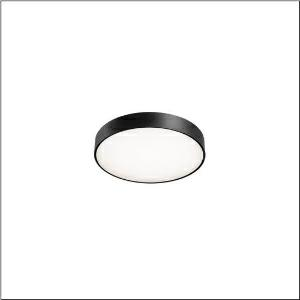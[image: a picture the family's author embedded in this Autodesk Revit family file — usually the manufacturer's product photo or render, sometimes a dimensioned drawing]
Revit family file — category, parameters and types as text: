
# Revit family: round_21_s_51mr34gd0421b
name_source: partatom
category: Lighting Fixtures
units: mm (PartAtom-declared; Revit-internal decimal feet)

## family parameters
Cut with Voids When Loaded = No
Host = Face
Light Source = No
Part Type = Normal
Room Calculation Point = No
Round Connector Dimension = Use Diameter
Shared = No

## types (1)
- Round 21 S (1 x LED, 4090 lm, 28.3 W, 4000K)
    Apparent Load = 28 VA
    CIE Flux Codes = 49 80 96 79 100
    Color Rendering = 80
    Color Temperature = 4000K
    Default Elevation = 1800 mm
    Description = Round 21 S, wall and ceiling luminaire, primary optical cover: cover, of PMMA, opal, light emission: direct/indirect distribution, primary light characteristic: symmetric, installation type: suspended mounting, surface-mounted, LED, rated luminous flux: 4.090lm, luminous efficacy: 135lm/W, light colour: 840, colour temperature: 4000K, control gear: DALI 2, with terminal, 5-pole, mains connection: 230V, AC, 50/60Hz, rated input power: 28.3W, housing, of aluminium, coated, black, diameter: 400mm, height: 62mm, protection rating (complete): IP40, insulation class (complete): insulation class I (protective earthing), certification: CE, impact resistance: IK04, permissible operating ambient temperature: -10..+35°C, packaging unit: 1 piece
    Height = 87 mm
    Lamp = 1 x LED
    Lamp Light Flux = 4090 lm
    Lamp Power = 28.3 W
    Lamp count = 1
    Length = 400 mm
    Luminous efficacy = 145 lm/W
    Manufacturer = Siteco
    ModVariant = No
    Model = 51MR34GD0421B
    Mounting Place = Wall
    Mounting Type = Surface mounted
    Number of Poles = 1
    OnlyDefault = Yes
    Power Factor = 1
    Product Name = Round 21 S
    Product group = wall and ceiling luminaire
    ProductGroupID = 2001
    Protection Class = Protection class I
    Protection Degree = IP 40
    RLX_Detail_Level = 1
    RLX_Emergency_Light_Flux = 0 lm
    RLX_Emergency_Type = 0
    RLX_Emergency_Type_DB = No
    RlxData = <blob elided: 13877 chars, md5=81fe5c87>
    Socket = socket
    Standby Power = 0 W
    System Light Flux = 4090 lm
    System Power = 28 W
    Type Comments = Product without accessories
    Type Image = l_1258311.jpg
    URL = http://relux.com
    VarID = ---
    Voltage = 0 V
    Weight = 0.00 kg
    Width = 0 mm  [stored 0 ft]

note: [stored X ft] marks values corroborated as IEEE doubles in the binary element streams (Revit-internal decimal feet)

## geometry (parser evidence)
native form markers: Sweep x11
no freeform markers — native parametric forms only
